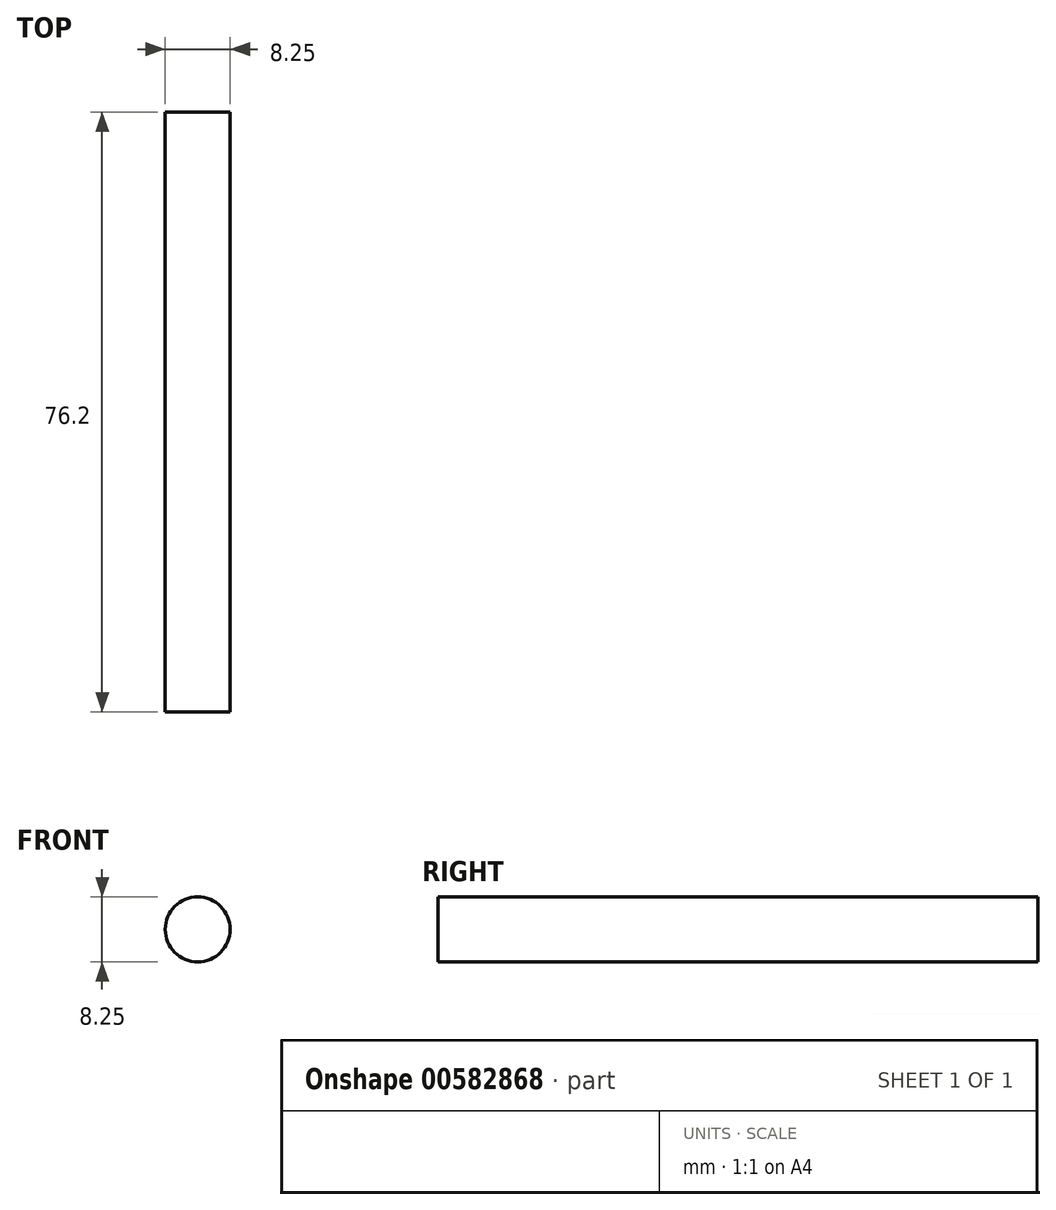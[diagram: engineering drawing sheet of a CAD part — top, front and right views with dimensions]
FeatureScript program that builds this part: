
annotation { "Feature Type Name" : "Feature", "Feature Type Description" : "" }
export const myFeature = defineFeature(function(context is Context, id is Id, definition is map)
    precondition{}
    {
        {
            var Q0;
            Q0=qCreatedBy(makeId("Front.planeOp"),FACE);
            var sketch = newSketch(context, id + "F0", { "sketchPlane" : qUnion([Q0])});
            skCircle(sketch, "E0", {"center": v(-29.73, 17.51) * mm, "radius": 4.13 * mm});
            skSolve(sketch);
        }
        {
            var Q0;
            Q0 = qSketchRegion(id + "F0", true);
            extrude(context, id + "F1", {"entities" : qUnion([Q0]), "depth" : 76.2 * mm, "offsetDistance" : 25.4 * mm});
        }
    });
